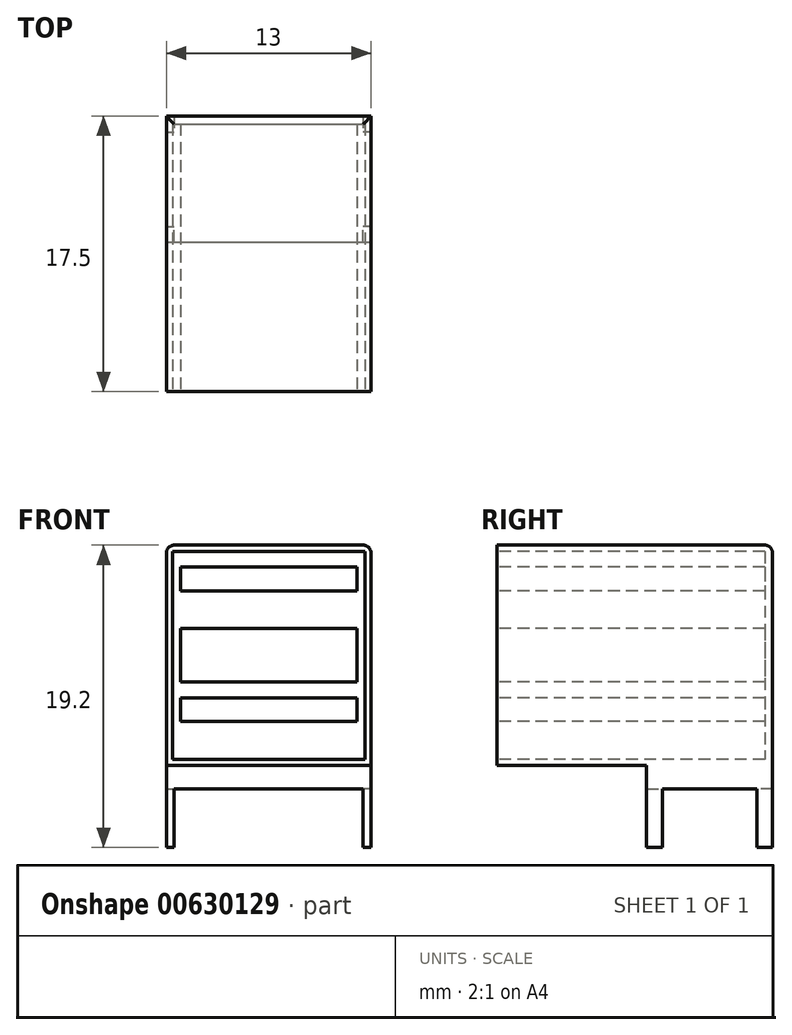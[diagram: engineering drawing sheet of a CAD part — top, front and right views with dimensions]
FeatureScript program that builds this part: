
annotation { "Feature Type Name" : "Feature", "Feature Type Description" : "" }
export const myFeature = defineFeature(function(context is Context, id is Id, definition is map)
    precondition{}
    {
        {
            var Q0;
            Q0=qCreatedBy(makeId("Front.planeOp"),FACE);
            var sketch = newSketch(context, id + "F0", { "sketchPlane" : qUnion([Q0])});
            skLineSegment(sketch, "E0.bottom", {"start": v(0, 0) * mm, "end": v(13, 0) * mm});
            skLineSegment(sketch, "E0.top", {"start": v(0, 14) * mm, "end": v(13, 14) * mm});
            skLineSegment(sketch, "E0.left", {"start": v(0, 0) * mm, "end": v(0, 14) * mm});
            skLineSegment(sketch, "E0.right", {"start": v(13, 0) * mm, "end": v(13, 14) * mm});
            skSolve(sketch);
        }
        {
            var Q0;
            Q0=qSketchRegion(id+"F0",true);
            extrude(context, id + "F1", {"entities" : qUnion([Q0]), "depth" : 17.5 * mm});
        }
        {
            var Q0;
            Q0=makeQuery(id+"F1.opExtrude","CAP_FACE",FACE,{"disambiguationData":[OSD([sQuery(id+"F0.wireOp",EDGE,"E0.bottom"),sQuery(id+"F0.wireOp",EDGE,"E0.top"),sQuery(id+"F0.wireOp",EDGE,"E0.left"),sQuery(id+"F0.wireOp",EDGE,"E0.right")])],"isStart":false});
            var sketch = newSketch(context, id + "F2", { "sketchPlane" : qUnion([Q0])});
            skLineSegment(sketch, "E1.bottom", {"start": v(0.4, 13.6) * mm, "end": v(12.6, 13.6) * mm});
            skLineSegment(sketch, "E1.top", {"start": v(0.4, 0.4) * mm, "end": v(12.6, 0.4) * mm});
            skLineSegment(sketch, "E1.left", {"start": v(0.4, 13.6) * mm, "end": v(0.4, 0.4) * mm});
            skLineSegment(sketch, "E1.right", {"start": v(12.6, 13.6) * mm, "end": v(12.6, 0.4) * mm});
            skLineSegment(sketch, "E2", {"start": v(6.5, 13.6) * mm, "end": v(6.5, 0.4) * mm, "construction": true});
            skLineSegment(sketch, "E3", {"start": v(0.4, 7) * mm, "end": v(12.6, 7) * mm, "construction": true});
            skLineSegment(sketch, "E4.bottom", {"start": v(0.9, 8.7) * mm, "end": v(12.1, 8.7) * mm});
            skLineSegment(sketch, "E4.top", {"start": v(0.9, 5.3) * mm, "end": v(12.1, 5.3) * mm});
            skLineSegment(sketch, "E4.left", {"start": v(0.9, 8.7) * mm, "end": v(0.9, 5.3) * mm});
            skLineSegment(sketch, "E4.right", {"start": v(12.1, 8.7) * mm, "end": v(12.1, 5.3) * mm});
            skLineSegment(sketch, "E5.bottom", {"start": v(0.9, 12.6) * mm, "end": v(12.1, 12.6) * mm});
            skLineSegment(sketch, "E5.top", {"start": v(0.9, 11.1) * mm, "end": v(12.1, 11.1) * mm});
            skLineSegment(sketch, "E5.left", {"start": v(0.9, 12.6) * mm, "end": v(0.9, 11.1) * mm});
            skLineSegment(sketch, "E5.right", {"start": v(12.1, 12.6) * mm, "end": v(12.1, 11.1) * mm});
            skLineSegment(sketch, "E6.bottom", {"start": v(0.9, 4.3) * mm, "end": v(12.1, 4.3) * mm});
            skLineSegment(sketch, "E6.top", {"start": v(0.9, 2.8) * mm, "end": v(12.1, 2.8) * mm});
            skLineSegment(sketch, "E6.left", {"start": v(0.9, 4.3) * mm, "end": v(0.9, 2.8) * mm});
            skLineSegment(sketch, "E6.right", {"start": v(12.1, 4.3) * mm, "end": v(12.1, 2.8) * mm});
            skSolve(sketch);
        }
        {
            var Q0;
            Q0=qSketchRegion(id+"F2",true);
            extrude(context, id + "F3", {"entities" : qUnion([Q0]), "operationType" : NewBodyOperationType.REMOVE, "oppositeDirection" : true, "depth" : 17 * mm});
        }
        {
            var Q0;
            Q0=makeQuery(id+"F1.opExtrude","SWEPT_FACE",FACE,{"disambiguationData":[OSD([sQuery(id+"F0.wireOp",EDGE,"E0.bottom")])]});
            var sketch = newSketch(context, id + "F4", { "sketchPlane" : qUnion([Q0])});
            skLineSegment(sketch, "E7.bottom", {"start": v(0, 0) * mm, "end": v(13, 0) * mm});
            skLineSegment(sketch, "E7.top", {"start": v(0, 8) * mm, "end": v(13, 8) * mm});
            skLineSegment(sketch, "E7.left", {"start": v(0, 0) * mm, "end": v(0, 8) * mm});
            skLineSegment(sketch, "E7.right", {"start": v(13, 0) * mm, "end": v(13, 8) * mm});
            skSolve(sketch);
        }
        {
            var Q0;
            Q0=qSketchRegion(id+"F4",true);
            extrude(context, id + "F5", {"entities" : qUnion([Q0]), "operationType" : NewBodyOperationType.ADD, "depth" : 1.5 * mm});
        }
        {
            var Q0;
            Q0=makeQuery(id+"F5.opExtrude","CAP_FACE",FACE,{"disambiguationData":[OSD([sQuery(id+"F4.wireOp",EDGE,"E7.bottom"),sQuery(id+"F4.wireOp",EDGE,"E7.top"),sQuery(id+"F4.wireOp",EDGE,"E7.left"),sQuery(id+"F4.wireOp",EDGE,"E7.right")])],"isStart":false});
            var sketch = newSketch(context, id + "F6", { "sketchPlane" : qUnion([Q0])});
            skLineSegment(sketch, "E8.bottom", {"start": v(0, 8) * mm, "end": v(0.5, 8) * mm});
            skLineSegment(sketch, "E8.top", {"start": v(0, 7) * mm, "end": v(0.5, 7) * mm});
            skLineSegment(sketch, "E8.left", {"start": v(0, 8) * mm, "end": v(0, 7) * mm});
            skLineSegment(sketch, "E8.right", {"start": v(0.5, 8) * mm, "end": v(0.5, 7) * mm});
            skLineSegment(sketch, "E9.bottom", {"start": v(0, 0) * mm, "end": v(0.5, 0) * mm});
            skLineSegment(sketch, "E9.top", {"start": v(0, 1) * mm, "end": v(0.5, 1) * mm});
            skLineSegment(sketch, "E9.left", {"start": v(0, 0) * mm, "end": v(0, 1) * mm});
            skLineSegment(sketch, "E9.right", {"start": v(0.5, 0) * mm, "end": v(0.5, 1) * mm});
            skLineSegment(sketch, "E10.bottom", {"start": v(13, 8) * mm, "end": v(12.5, 8) * mm});
            skLineSegment(sketch, "E10.top", {"start": v(13, 7) * mm, "end": v(12.5, 7) * mm});
            skLineSegment(sketch, "E10.left", {"start": v(13, 8) * mm, "end": v(13, 7) * mm});
            skLineSegment(sketch, "E10.right", {"start": v(12.5, 8) * mm, "end": v(12.5, 7) * mm});
            skLineSegment(sketch, "E11.bottom", {"start": v(13, 0) * mm, "end": v(12.5, 0) * mm});
            skLineSegment(sketch, "E11.top", {"start": v(13, 1) * mm, "end": v(12.5, 1) * mm});
            skLineSegment(sketch, "E11.left", {"start": v(13, 0) * mm, "end": v(13, 1) * mm});
            skLineSegment(sketch, "E11.right", {"start": v(12.5, 0) * mm, "end": v(12.5, 1) * mm});
            skSolve(sketch);
        }
        {
            var Q0;
            Q0=qSketchRegion(id+"F6",true);
            extrude(context, id + "F7", {"entities" : qUnion([Q0]), "operationType" : NewBodyOperationType.ADD, "depth" : 3.7 * mm});
        }
        {
            var Q0;
            Q0=makeQuery(id+"F1.opExtrude","SWEPT_EDGE",EDGE,{"disambiguationData":[OSD([sQuery(id+"F0.wireOp",EDGE,"E0.top"),sQuery(id+"F0.wireOp",EDGE,"E0.right")])]});
            var Q1;
            Q1=makeQuery(id+"F1.opExtrude","CAP_EDGE",EDGE,{"disambiguationData":[OSD([sQuery(id+"F0.wireOp",EDGE,"E0.top")])],"isStart":true});
            var Q2;
            Q2=makeQuery(id+"F1.opExtrude","SWEPT_EDGE",EDGE,{"disambiguationData":[OSD([sQuery(id+"F0.wireOp",EDGE,"E0.top"),sQuery(id+"F0.wireOp",EDGE,"E0.left")])]});
            fillet(context, id + "F8", {"entities" : qUnion([Q0, Q1, Q2]), "radius" : 0.5 * mm, "tangentPropagation" : true, "allowEdgeOverflow" : false});
        }
    });
